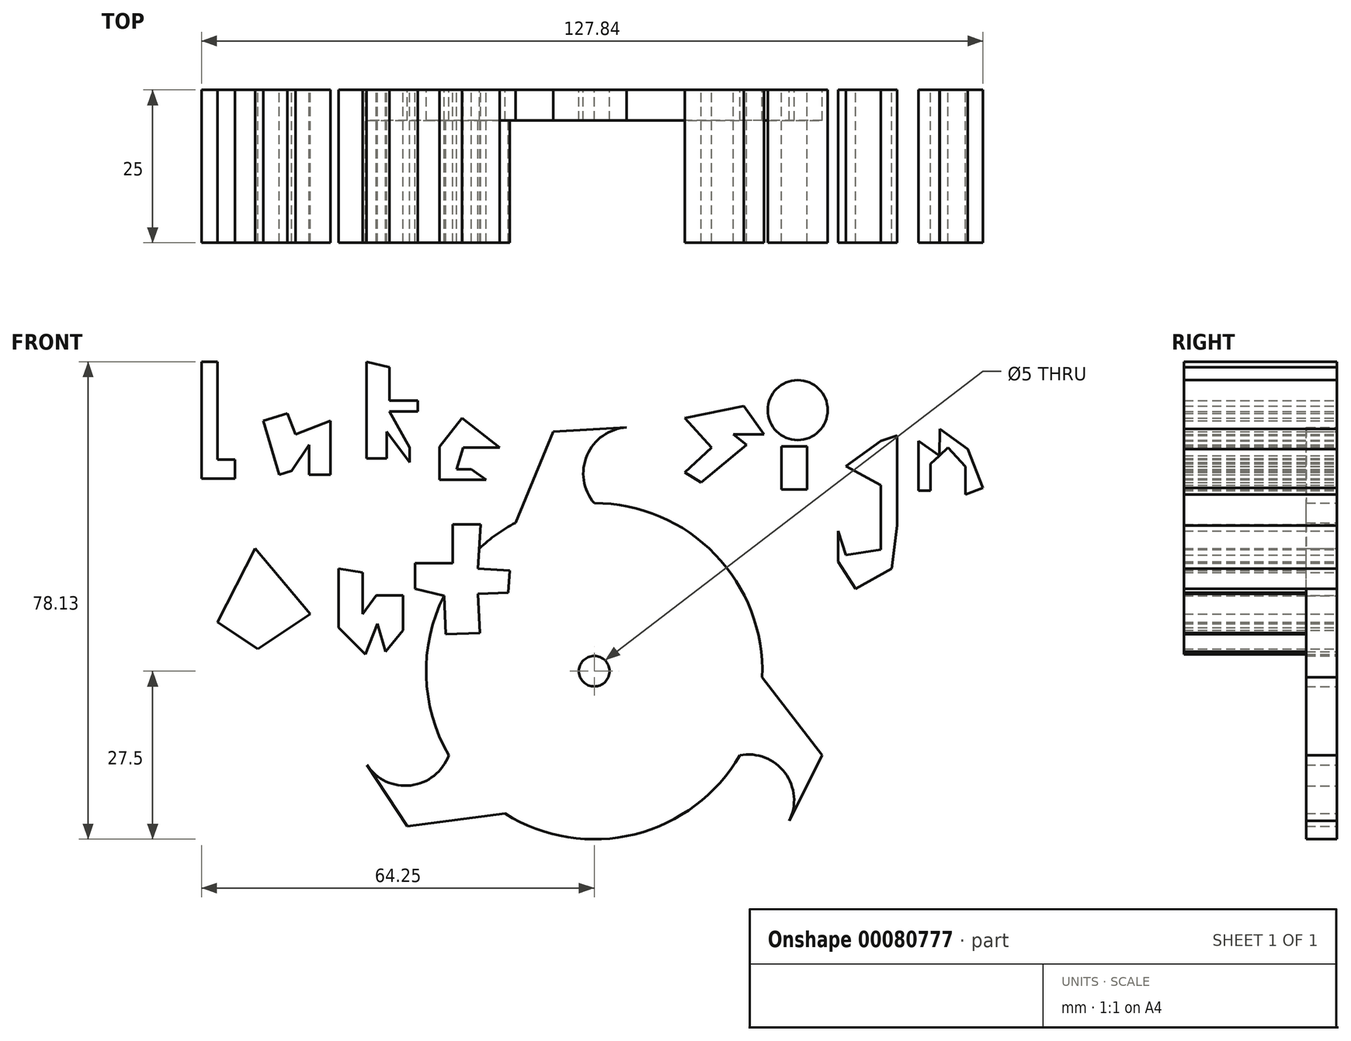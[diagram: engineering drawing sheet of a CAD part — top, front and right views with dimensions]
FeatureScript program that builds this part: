
annotation { "Feature Type Name" : "Feature", "Feature Type Description" : "" }
export const myFeature = defineFeature(function(context is Context, id is Id, definition is map)
    precondition{}
    {
        {
            var Q0;
            Q0=qCreatedBy(makeId("Front.planeOp"),FACE);
            var sketch = newSketch(context, id + "F0", { "sketchPlane" : qUnion([Q0])});
            skCircle(sketch, "E0", {"center": v(0, 0) * mm, "radius": 27.5 * mm});
            skLineSegment(sketch, "E1", {"start": v(-12.9, 24.29) * mm, "end": v(-6.7, 39.17) * mm});
            skLineSegment(sketch, "E2", {"start": v(-6.7, 39.17) * mm, "end": v(5.29, 39.88) * mm});
            skCircle(sketch, "E3", {"center": v(0, 0) * mm, "radius": 2.5 * mm});
            skArc(sketch, "E4", {"start": v(5.29, 39.88) * mm, "mid": v(-1.19, 35.33) * mm, "end": v(0, 27.5) * mm});
            skLineSegment(sketch, "E5.1.0", {"start": v(-30.57, -25.4) * mm, "end": v(-37.18, -15.36) * mm});
            skLineSegment(sketch, "E5.1.1", {"start": v(-14.59, -23.31) * mm, "end": v(-30.57, -25.4) * mm});
            skArc(sketch, "E5.1.2", {"start": v(-37.18, -15.36) * mm, "mid": v(-30, -18.7) * mm, "end": v(-23.82, -13.75) * mm});
            skLineSegment(sketch, "E5.2.0", {"start": v(37.28, -13.78) * mm, "end": v(31.9, -24.52) * mm});
            skLineSegment(sketch, "E5.2.1", {"start": v(27.48, -0.98) * mm, "end": v(37.28, -13.78) * mm});
            skArc(sketch, "E5.2.2", {"start": v(31.9, -24.52) * mm, "mid": v(31.19, -16.64) * mm, "end": v(23.82, -13.75) * mm});
            skSolve(sketch);
        }
        {
            var Q0;
            Q0=makeQuery(id+"F0.imprint","IMPRINT",FACE,{"disambiguationData":[TD([[makeQuery(id+"F0.imprint","IMPRINT",EDGE,{"derivedFrom":sQuery(id+"F0.wireOp",EDGE,"E3")}),-1.0]])]});
            var Q1;
            {var subQ0=sQuery(id+"F0.wireOp",EDGE,"E1");Q1=makeQuery(id+"F0.imprint","IMPRINT",FACE,{"disambiguationData":[TD([[makeQuery(id+"F0.imprint","IMPRINT",EDGE,{"derivedFrom":subQ0}),-1.0]])]});}
            var Q2;
            Q2=makeQuery(id+"F0.imprint","IMPRINT",FACE,{"disambiguationData":[TD([[makeQuery(id+"F0.imprint","IMPRINT",EDGE,{"derivedFrom":sQuery(id+"F0.wireOp",EDGE,"E5.1.0")}),-1.0]])]});
            var Q3;
            Q3=makeQuery(id+"F0.imprint","IMPRINT",FACE,{"disambiguationData":[TD([[makeQuery(id+"F0.imprint","IMPRINT",EDGE,{"derivedFrom":sQuery(id+"F0.wireOp",EDGE,"E5.2.0")}),-1.0]])]});
            extrude(context, id + "F1", {"entities" : qUnion([Q0, Q1, Q2, Q3]), "depth" : 5 * mm});
        }
        {
            var Q0;
            Q0=qCreatedBy(makeId("Front.planeOp"),FACE);
            var sketch = newSketch(context, id + "F2", { "sketchPlane" : qUnion([Q0])});
            skLineSegment(sketch, "E6", {"start": v(-64.25, 50.63) * mm, "end": v(-64.25, 31.52) * mm});
            skLineSegment(sketch, "E7", {"start": v(-64.25, 31.52) * mm, "end": v(-58.76, 31.52) * mm});
            skLineSegment(sketch, "E8", {"start": v(-58.76, 31.52) * mm, "end": v(-58.76, 34.6) * mm});
            skLineSegment(sketch, "E9", {"start": v(-58.76, 34.6) * mm, "end": v(-61.62, 34.6) * mm});
            skLineSegment(sketch, "E10", {"start": v(-61.62, 34.6) * mm, "end": v(-61.62, 50.63) * mm});
            skLineSegment(sketch, "E11", {"start": v(-61.62, 50.63) * mm, "end": v(-64.25, 50.63) * mm});
            skLineSegment(sketch, "E12", {"start": v(-54.15, 40.97) * mm, "end": v(-51.51, 32.18) * mm});
            skLineSegment(sketch, "E13", {"start": v(-51.51, 32.18) * mm, "end": v(-49.5, 32.79) * mm});
            skLineSegment(sketch, "E14", {"start": v(-49.5, 32.79) * mm, "end": v(-46.68, 37.01) * mm});
            skLineSegment(sketch, "E15", {"start": v(-46.68, 37.01) * mm, "end": v(-46.68, 32.18) * mm});
            skLineSegment(sketch, "E16", {"start": v(-46.68, 32.18) * mm, "end": v(-43.16, 32.18) * mm});
            skLineSegment(sketch, "E17", {"start": v(-43.16, 32.18) * mm, "end": v(-43.16, 40.97) * mm});
            skLineSegment(sketch, "E18", {"start": v(-43.16, 40.97) * mm, "end": v(-48.88, 38.77) * mm});
            skLineSegment(sketch, "E19", {"start": v(-48.88, 38.77) * mm, "end": v(-50.19, 42.19) * mm});
            skLineSegment(sketch, "E20", {"start": v(-50.19, 42.19) * mm, "end": v(-54.15, 40.97) * mm});
            skLineSegment(sketch, "E21", {"start": v(-37.23, 50.63) * mm, "end": v(-37.23, 34.82) * mm});
            skLineSegment(sketch, "E22", {"start": v(-37.23, 34.82) * mm, "end": v(-33.94, 34.82) * mm});
            skLineSegment(sketch, "E23", {"start": v(-33.94, 34.82) * mm, "end": v(-33.94, 39.21) * mm});
            skLineSegment(sketch, "E24", {"start": v(-33.94, 39.21) * mm, "end": v(-30.2, 34.16) * mm});
            skLineSegment(sketch, "E25", {"start": v(-30.2, 34.16) * mm, "end": v(-30.2, 36.57) * mm});
            skLineSegment(sketch, "E26", {"start": v(-30.2, 36.57) * mm, "end": v(-33.5, 42.5) * mm});
            skLineSegment(sketch, "E27", {"start": v(-33.5, 42.5) * mm, "end": v(-28.89, 42.5) * mm});
            skLineSegment(sketch, "E28", {"start": v(-28.89, 42.5) * mm, "end": v(-28.89, 44.26) * mm});
            skLineSegment(sketch, "E29", {"start": v(-28.89, 44.26) * mm, "end": v(-33.5, 44.26) * mm});
            skLineSegment(sketch, "E30", {"start": v(-33.5, 44.26) * mm, "end": v(-33.5, 49.75) * mm});
            skLineSegment(sketch, "E31", {"start": v(-33.5, 49.75) * mm, "end": v(-37.23, 50.63) * mm});
            skLineSegment(sketch, "E32", {"start": v(-21.42, 36.57) * mm, "end": v(-15.49, 36.57) * mm});
            skLineSegment(sketch, "E33", {"start": v(-15.49, 36.57) * mm, "end": v(-21.64, 41.4) * mm});
            skLineSegment(sketch, "E34", {"start": v(-21.64, 41.4) * mm, "end": v(-25.3, 36.75) * mm});
            skLineSegment(sketch, "E35", {"start": v(-25.3, 36.75) * mm, "end": v(-25.3, 31.3) * mm});
            skLineSegment(sketch, "E36", {"start": v(-25.3, 31.3) * mm, "end": v(-20.1, 31.3) * mm});
            skLineSegment(sketch, "E37", {"start": v(-20.1, 31.3) * mm, "end": v(-17.68, 31.3) * mm});
            skLineSegment(sketch, "E38", {"start": v(-17.68, 31.3) * mm, "end": v(-20.1, 33.06) * mm});
            skLineSegment(sketch, "E39", {"start": v(-20.1, 33.06) * mm, "end": v(-22.52, 33.06) * mm});
            skLineSegment(sketch, "E40", {"start": v(-22.52, 33.06) * mm, "end": v(-21.42, 36.57) * mm});
            skLineSegment(sketch, "E41", {"start": v(24.5, 43.38) * mm, "end": v(14.83, 41.4) * mm});
            skLineSegment(sketch, "E42", {"start": v(14.83, 41.4) * mm, "end": v(19.22, 36.57) * mm});
            skLineSegment(sketch, "E43", {"start": v(19.22, 36.57) * mm, "end": v(14.8, 32.56) * mm});
            skLineSegment(sketch, "E44", {"start": v(14.8, 32.56) * mm, "end": v(17.46, 30.86) * mm});
            skLineSegment(sketch, "E45", {"start": v(17.46, 30.86) * mm, "end": v(24.93, 37.01) * mm});
            skLineSegment(sketch, "E46", {"start": v(24.93, 37.01) * mm, "end": v(22.74, 38.77) * mm});
            skLineSegment(sketch, "E47", {"start": v(22.74, 38.77) * mm, "end": v(27.79, 38.77) * mm});
            skLineSegment(sketch, "E48", {"start": v(27.79, 38.77) * mm, "end": v(24.5, 43.38) * mm});
            skLineSegment(sketch, "E49", {"start": v(30.64, 36.8) * mm, "end": v(30.64, 29.76) * mm});
            skLineSegment(sketch, "E50", {"start": v(30.64, 29.76) * mm, "end": v(34.82, 29.76) * mm});
            skLineSegment(sketch, "E51", {"start": v(34.82, 29.76) * mm, "end": v(34.82, 36.8) * mm});
            skLineSegment(sketch, "E52", {"start": v(34.82, 36.8) * mm, "end": v(30.64, 36.8) * mm});
            skLineSegment(sketch, "E53", {"start": v(31.08, 42.29) * mm, "end": v(31.08, 39.65) * mm});
            skLineSegment(sketch, "E54", {"start": v(31.08, 39.65) * mm, "end": v(33.28, 40.53) * mm});
            skLineSegment(sketch, "E55", {"start": v(33.28, 40.53) * mm, "end": v(33.28, 42.72) * mm});
            skLineSegment(sketch, "E56", {"start": v(33.28, 42.72) * mm, "end": v(31.08, 42.72) * mm});
            skLineSegment(sketch, "E57", {"start": v(31.08, 42.72) * mm, "end": v(33.28, 42.72) * mm});
            skLineSegment(sketch, "E58", {"start": v(46.9, 37.67) * mm, "end": v(41.16, 33.58) * mm});
            skLineSegment(sketch, "E59", {"start": v(41.16, 33.58) * mm, "end": v(46.9, 30.42) * mm});
            skLineSegment(sketch, "E60", {"start": v(46.9, 30.42) * mm, "end": v(46.9, 19.88) * mm});
            skLineSegment(sketch, "E61", {"start": v(46.9, 19.88) * mm, "end": v(41.19, 19) * mm});
            skLineSegment(sketch, "E62", {"start": v(41.19, 19) * mm, "end": v(39.87, 22.96) * mm});
            skLineSegment(sketch, "E63", {"start": v(39.87, 22.96) * mm, "end": v(39.87, 17.9) * mm});
            skLineSegment(sketch, "E64", {"start": v(39.87, 17.9) * mm, "end": v(42.72, 13.5) * mm});
            skLineSegment(sketch, "E65", {"start": v(42.72, 13.5) * mm, "end": v(48.66, 16.8) * mm});
            skLineSegment(sketch, "E66", {"start": v(48.66, 16.8) * mm, "end": v(49.53, 23.83) * mm});
            skLineSegment(sketch, "E67", {"start": v(49.53, 23.83) * mm, "end": v(49.53, 38.55) * mm});
            skLineSegment(sketch, "E68", {"start": v(49.53, 38.55) * mm, "end": v(46.9, 37.67) * mm});
            skLineSegment(sketch, "E69", {"start": v(53.05, 37.67) * mm, "end": v(53.05, 29.54) * mm});
            skLineSegment(sketch, "E70", {"start": v(53.05, 29.54) * mm, "end": v(55.03, 29.54) * mm});
            skLineSegment(sketch, "E71", {"start": v(55.03, 29.54) * mm, "end": v(55.03, 33.94) * mm});
            skLineSegment(sketch, "E72", {"start": v(55.03, 33.94) * mm, "end": v(57.88, 36.57) * mm});
            skLineSegment(sketch, "E73", {"start": v(57.88, 36.57) * mm, "end": v(60.73, 33.5) * mm});
            skLineSegment(sketch, "E74", {"start": v(60.73, 33.5) * mm, "end": v(60.74, 28.89) * mm});
            skLineSegment(sketch, "E75", {"start": v(60.74, 28.89) * mm, "end": v(63.6, 29.98) * mm});
            skLineSegment(sketch, "E76", {"start": v(63.6, 29.98) * mm, "end": v(61.14, 36.36) * mm});
            skLineSegment(sketch, "E77", {"start": v(61.14, 36.36) * mm, "end": v(56.56, 39.65) * mm});
            skLineSegment(sketch, "E78", {"start": v(56.56, 39.65) * mm, "end": v(56.45, 35.26) * mm});
            skLineSegment(sketch, "E79", {"start": v(56.45, 35.26) * mm, "end": v(53.05, 37.67) * mm});
            skLineSegment(sketch, "E80", {"start": v(-55.47, 20.1) * mm, "end": v(-61.62, 8.02) * mm});
            skLineSegment(sketch, "E81", {"start": v(-61.62, 8.02) * mm, "end": v(-55.03, 3.62) * mm});
            skLineSegment(sketch, "E82", {"start": v(-55.03, 3.62) * mm, "end": v(-46.46, 9.34) * mm});
            skLineSegment(sketch, "E83", {"start": v(-46.46, 9.34) * mm, "end": v(-55.47, 20.1) * mm});
            skLineSegment(sketch, "E84", {"start": v(-41.85, 16.8) * mm, "end": v(-41.85, 7.14) * mm});
            skLineSegment(sketch, "E85", {"start": v(-41.85, 7.14) * mm, "end": v(-37.45, 2.75) * mm});
            skLineSegment(sketch, "E86", {"start": v(-37.45, 2.75) * mm, "end": v(-35.48, 7.8) * mm});
            skLineSegment(sketch, "E87", {"start": v(-35.48, 7.8) * mm, "end": v(-34.16, 3.19) * mm});
            skLineSegment(sketch, "E88", {"start": v(-34.16, 3.19) * mm, "end": v(-31.3, 6.7) * mm});
            skLineSegment(sketch, "E89", {"start": v(-31.3, 6.7) * mm, "end": v(-31.3, 12.41) * mm});
            skLineSegment(sketch, "E90", {"start": v(-31.3, 12.41) * mm, "end": v(-35.7, 12.41) * mm});
            skLineSegment(sketch, "E91", {"start": v(-35.7, 12.41) * mm, "end": v(-37.9, 9.34) * mm});
            skLineSegment(sketch, "E92", {"start": v(-37.9, 9.34) * mm, "end": v(-37.9, 16.15) * mm});
            skLineSegment(sketch, "E93", {"start": v(-37.9, 16.15) * mm, "end": v(-41.85, 16.8) * mm});
            skLineSegment(sketch, "E94", {"start": v(-29.33, 13.5) * mm, "end": v(-29.33, 17.68) * mm});
            skLineSegment(sketch, "E95", {"start": v(-29.33, 17.68) * mm, "end": v(-23.17, 17.68) * mm});
            skLineSegment(sketch, "E96", {"start": v(-23.17, 17.68) * mm, "end": v(-23.17, 24.05) * mm});
            skLineSegment(sketch, "E97", {"start": v(-23.17, 24.05) * mm, "end": v(-18.56, 24.05) * mm});
            skLineSegment(sketch, "E98", {"start": v(-18.56, 24.05) * mm, "end": v(-19, 16.8) * mm});
            skLineSegment(sketch, "E99", {"start": v(-19, 16.8) * mm, "end": v(-13.83, 16.5) * mm});
            skLineSegment(sketch, "E100", {"start": v(-13.83, 16.5) * mm, "end": v(-14.05, 12.84) * mm});
            skLineSegment(sketch, "E101", {"start": v(-14.05, 12.84) * mm, "end": v(-19, 12.63) * mm});
            skLineSegment(sketch, "E102", {"start": v(-19, 12.63) * mm, "end": v(-18.73, 6.27) * mm});
            skLineSegment(sketch, "E103", {"start": v(-18.73, 6.27) * mm, "end": v(-24.28, 6.03) * mm});
            skLineSegment(sketch, "E104", {"start": v(-24.28, 6.03) * mm, "end": v(-24.55, 12.36) * mm});
            skLineSegment(sketch, "E105", {"start": v(-24.55, 12.36) * mm, "end": v(-29.33, 13.5) * mm});
            skCircle(sketch, "E106", {"center": v(33.28, 42.72) * mm, "radius": 4.9 * mm});
            skSolve(sketch);
        }
        {
            var Q0;
            Q0=makeQuery(id+"F2.imprint","IMPRINT",FACE,{"disambiguationData":[TD([[makeQuery(id+"F2.imprint","IMPRINT",EDGE,{"derivedFrom":sQuery(id+"F2.wireOp",EDGE,"E6")}),1.0]])]});
            var Q1;
            Q1=makeQuery(id+"F2.imprint","IMPRINT",FACE,{"disambiguationData":[TD([[makeQuery(id+"F2.imprint","IMPRINT",EDGE,{"derivedFrom":sQuery(id+"F2.wireOp",EDGE,"E12")}),1.0]])]});
            var Q2;
            Q2=makeQuery(id+"F2.imprint","IMPRINT",FACE,{"disambiguationData":[TD([[makeQuery(id+"F2.imprint","IMPRINT",EDGE,{"derivedFrom":sQuery(id+"F2.wireOp",EDGE,"E21")}),1.0]])]});
            var Q3;
            Q3=makeQuery(id+"F2.imprint","IMPRINT",FACE,{"disambiguationData":[TD([[makeQuery(id+"F2.imprint","IMPRINT",EDGE,{"derivedFrom":sQuery(id+"F2.wireOp",EDGE,"E32")}),1.0]])]});
            var Q4;
            Q4=makeQuery(id+"F2.imprint","IMPRINT",FACE,{"disambiguationData":[TD([[makeQuery(id+"F2.imprint","IMPRINT",EDGE,{"derivedFrom":sQuery(id+"F2.wireOp",EDGE,"E41")}),1.0]])]});
            var Q5;
            Q5=makeQuery(id+"F2.imprint","IMPRINT",FACE,{"disambiguationData":[TD([[makeQuery(id+"F2.imprint","IMPRINT",EDGE,{"derivedFrom":sQuery(id+"F2.wireOp",EDGE,"E49")}),1.0]])]});
            var Q6;
            Q6=makeQuery(id+"F2.imprint","IMPRINT",FACE,{"disambiguationData":[TD([[makeQuery(id+"F2.imprint","IMPRINT",EDGE,{"derivedFrom":sQuery(id+"F2.wireOp",EDGE,"E58")}),1.0]])]});
            var Q7;
            Q7=makeQuery(id+"F2.imprint","IMPRINT",FACE,{"disambiguationData":[TD([[makeQuery(id+"F2.imprint","IMPRINT",EDGE,{"derivedFrom":sQuery(id+"F2.wireOp",EDGE,"E69")}),1.0]])]});
            var Q8;
            {var subQ0=sQuery(id+"F2.wireOp",EDGE,"E73");Q8=makeQuery(id+"F2.imprint","IMPRINT",FACE,{"disambiguationData":[TD([[makeQuery(id+"F2.imprint","IMPRINT",EDGE,{"derivedFrom":subQ0}),1.0]])]});}
            var Q9;
            Q9=makeQuery(id+"F2.imprint","IMPRINT",FACE,{"disambiguationData":[TD([[makeQuery(id+"F2.imprint","IMPRINT",EDGE,{"derivedFrom":sQuery(id+"F2.wireOp",EDGE,"E94")}),-1.0]])]});
            var Q10;
            Q10=makeQuery(id+"F2.imprint","IMPRINT",FACE,{"disambiguationData":[TD([[makeQuery(id+"F2.imprint","IMPRINT",EDGE,{"derivedFrom":sQuery(id+"F2.wireOp",EDGE,"E84")}),1.0]])]});
            var Q11;
            Q11=makeQuery(id+"F2.imprint","IMPRINT",FACE,{"disambiguationData":[TD([[makeQuery(id+"F2.imprint","IMPRINT",EDGE,{"derivedFrom":sQuery(id+"F2.wireOp",EDGE,"E80")}),1.0]])]});
            extrude(context, id + "F3", {"entities" : qUnion([Q0, Q1, Q2, Q3, Q4, Q5, Q6, Q7, Q8, Q9, Q10, Q11]), "operationType" : NewBodyOperationType.ADD, "depth" : 25 * mm});
        }
        {
            var Q0;
            Q0=makeQuery(id+"F2.imprint","IMPRINT",FACE,{"disambiguationData":[TD([[makeQuery(id+"F2.imprint","IMPRINT",EDGE,{"derivedFrom":sQuery(id+"F2.wireOp",EDGE,"E106")}),1.0]])]});
            extrude(context, id + "F4", {"entities" : qUnion([Q0]), "depth" : 25 * mm});
        }
    });
